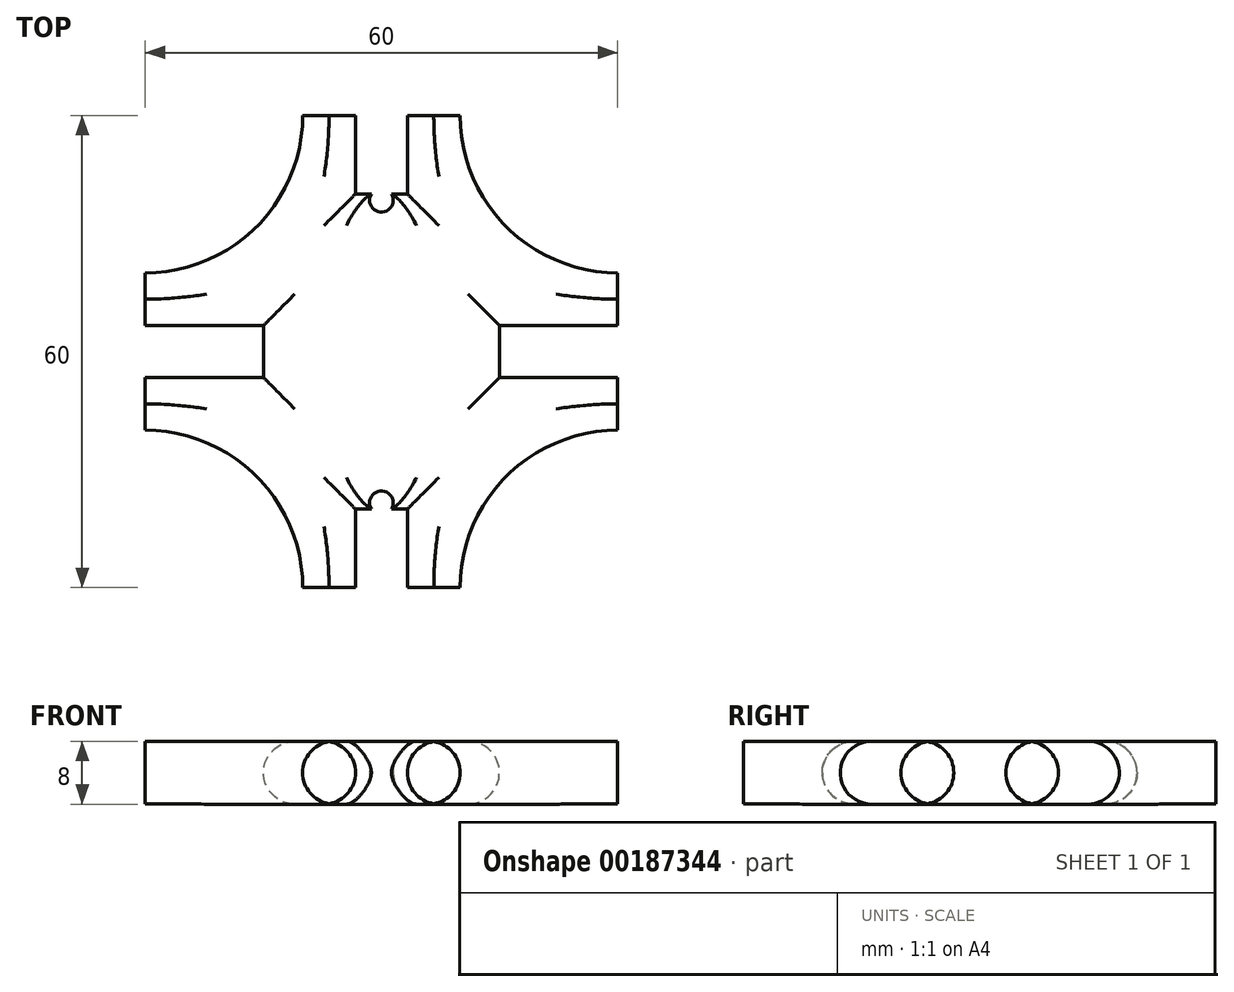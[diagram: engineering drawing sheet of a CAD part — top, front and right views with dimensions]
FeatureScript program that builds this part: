
annotation { "Feature Type Name" : "Feature", "Feature Type Description" : "" }
export const myFeature = defineFeature(function(context is Context, id is Id, definition is map)
    precondition{}
    {
        {
            var Q0;
            Q0=qCreatedBy(makeId("Top.planeOp"),FACE);
            var sketch = newSketch(context, id + "F0", { "sketchPlane" : qUnion([Q0])});
            skLineSegment(sketch, "E0.bottom", {"start": v(10, 30) * mm, "end": v(3.3, 30) * mm});
            skLineSegment(sketch, "E0.top", {"start": v(10, -30) * mm, "end": v(3.3, -30) * mm});
            skLineSegment(sketch, "E0.left", {"start": v(30, 10) * mm, "end": v(30, 3.3) * mm});
            skLineSegment(sketch, "E0.right", {"start": v(-30, 10) * mm, "end": v(-30, 3.3) * mm});
            skPoint(sketch, "E0.middle", {"position": v(0, 0) * mm});
            skArc(sketch, "E1", {"start": v(10, 30) * mm, "mid": v(15.86, 15.86) * mm, "end": v(30, 10) * mm});
            skArc(sketch, "E2", {"start": v(-30, 10) * mm, "mid": v(-15.86, 15.86) * mm, "end": v(-10, 30) * mm});
            skArc(sketch, "E3", {"start": v(-10, -30) * mm, "mid": v(-15.86, -15.86) * mm, "end": v(-30, -10) * mm});
            skArc(sketch, "E4", {"start": v(30, -10) * mm, "mid": v(15.86, -15.86) * mm, "end": v(10, -30) * mm});
            skLineSegment(sketch, "E5.top", {"start": v(-3.3, 20) * mm, "end": v(-1.28, 20) * mm});
            skLineSegment(sketch, "E5.left", {"start": v(-3.3, 30) * mm, "end": v(-3.3, 20) * mm});
            skLineSegment(sketch, "E5.right", {"start": v(3.3, 30) * mm, "end": v(3.3, 20) * mm});
            skArc(sketch, "E6", {"start": v(-1.28, 20) * mm, "mid": v(0, 17.72) * mm, "end": v(1.28, 20) * mm});
            skPoint(sketch, "E6.centerSnap0", {"position": v(0, 20) * mm});
            skLineSegment(sketch, "E7.trimOffspring", {"start": v(1.28, 20) * mm, "end": v(3.3, 20) * mm});
            skLineSegment(sketch, "E8.trimOffspring", {"start": v(-3.3, 30) * mm, "end": v(-10, 30) * mm});
            skLineSegment(sketch, "E9.bottom", {"start": v(3.3, -20) * mm, "end": v(1.28, -20) * mm});
            skLineSegment(sketch, "E9.left", {"start": v(3.3, -20) * mm, "end": v(3.3, -30) * mm});
            skLineSegment(sketch, "E9.right", {"start": v(-3.3, -20) * mm, "end": v(-3.3, -30) * mm});
            skPoint(sketch, "E9.middle", {"position": v(0, -30) * mm});
            skPoint(sketch, "E9.top.end.orphan", {"position": v(-3.3, -40) * mm});
            skPoint(sketch, "E9.top.start.orphan", {"position": v(3.3, -40) * mm});
            skLineSegment(sketch, "E10.trimOffspring", {"start": v(-3.3, -30) * mm, "end": v(-10, -30) * mm});
            skArc(sketch, "E11", {"start": v(1.28, -20) * mm, "mid": v(0, -17.72) * mm, "end": v(-1.28, -20) * mm});
            skLineSegment(sketch, "E12.trimOffspring", {"start": v(-1.28, -20) * mm, "end": v(-3.3, -20) * mm});
            skLineSegment(sketch, "E13.bottom", {"start": v(-15, 3.3) * mm, "end": v(-30, 3.3) * mm});
            skLineSegment(sketch, "E13.top", {"start": v(-15, -3.3) * mm, "end": v(-30, -3.3) * mm});
            skLineSegment(sketch, "E13.left", {"start": v(-15, 3.3) * mm, "end": v(-15, -3.3) * mm});
            skPoint(sketch, "E13.middle", {"position": v(-30, 0) * mm});
            skPoint(sketch, "E13.right.start.orphan", {"position": v(-45, 3.3) * mm});
            skPoint(sketch, "E14.orphan", {"position": v(-45, -3.3) * mm});
            skLineSegment(sketch, "E15.trimOffspring", {"start": v(-30, -3.3) * mm, "end": v(-30, -10) * mm});
            skLineSegment(sketch, "E16.bottom", {"start": v(15, -3.3) * mm, "end": v(30, -3.3) * mm});
            skLineSegment(sketch, "E16.top", {"start": v(15, 3.3) * mm, "end": v(30, 3.3) * mm});
            skLineSegment(sketch, "E16.left", {"start": v(15, -3.3) * mm, "end": v(15, 3.3) * mm});
            skPoint(sketch, "E16.middle", {"position": v(30, 0) * mm});
            skPoint(sketch, "E16.right.end.orphan", {"position": v(45, 3.3) * mm});
            skPoint(sketch, "E17.orphan", {"position": v(45, -3.3) * mm});
            skLineSegment(sketch, "E18.trimOffspring", {"start": v(30, -3.3) * mm, "end": v(30, -10) * mm});
            skSolve(sketch);
        }
        {
            var Q0;
            Q0=makeQuery(id+"F0.imprint","IMPRINT",FACE,{"disambiguationData":[TD([[makeQuery(id+"F0.imprint","IMPRINT",EDGE,{"derivedFrom":sQuery(id+"F0.wireOp",EDGE,"E0.bottom")}),1.0]])]});
            extrude(context, id + "F1", {"entities" : qUnion([Q0]), "depth" : 8 * mm});
        }
        {
            var Q0;
            Q0=makeQuery(id+"F1.opExtrude","CAP_FACE",FACE,{"disambiguationData":[OSD([sQuery(id+"F0.wireOp",EDGE,"E0.bottom"),sQuery(id+"F0.wireOp",EDGE,"E0.top"),sQuery(id+"F0.wireOp",EDGE,"E0.left"),sQuery(id+"F0.wireOp",EDGE,"E0.right"),sQuery(id+"F0.wireOp",EDGE,"E1"),sQuery(id+"F0.wireOp",EDGE,"E2"),sQuery(id+"F0.wireOp",EDGE,"E3"),sQuery(id+"F0.wireOp",EDGE,"E4"),sQuery(id+"F0.wireOp",EDGE,"E5.top"),sQuery(id+"F0.wireOp",EDGE,"E5.left"),sQuery(id+"F0.wireOp",EDGE,"E5.right"),sQuery(id+"F0.wireOp",EDGE,"E6"),sQuery(id+"F0.wireOp",EDGE,"E7.trimOffspring"),sQuery(id+"F0.wireOp",EDGE,"E8.trimOffspring"),sQuery(id+"F0.wireOp",EDGE,"E9.bottom"),sQuery(id+"F0.wireOp",EDGE,"E9.left"),sQuery(id+"F0.wireOp",EDGE,"E9.right"),sQuery(id+"F0.wireOp",EDGE,"E10.trimOffspring"),sQuery(id+"F0.wireOp",EDGE,"E11"),sQuery(id+"F0.wireOp",EDGE,"E12.trimOffspring"),sQuery(id+"F0.wireOp",EDGE,"E13.bottom"),sQuery(id+"F0.wireOp",EDGE,"E13.top"),sQuery(id+"F0.wireOp",EDGE,"E13.left"),sQuery(id+"F0.wireOp",EDGE,"E15.trimOffspring"),sQuery(id+"F0.wireOp",EDGE,"E16.bottom"),sQuery(id+"F0.wireOp",EDGE,"E16.top"),sQuery(id+"F0.wireOp",EDGE,"E16.left"),sQuery(id+"F0.wireOp",EDGE,"E18.trimOffspring")])],"isStart":false});
            var Q1;
            Q1=makeQuery(id+"F1.opExtrude","CAP_FACE",FACE,{"disambiguationData":[OSD([sQuery(id+"F0.wireOp",EDGE,"E0.bottom"),sQuery(id+"F0.wireOp",EDGE,"E0.top"),sQuery(id+"F0.wireOp",EDGE,"E0.left"),sQuery(id+"F0.wireOp",EDGE,"E0.right"),sQuery(id+"F0.wireOp",EDGE,"E1"),sQuery(id+"F0.wireOp",EDGE,"E2"),sQuery(id+"F0.wireOp",EDGE,"E3"),sQuery(id+"F0.wireOp",EDGE,"E4"),sQuery(id+"F0.wireOp",EDGE,"E5.top"),sQuery(id+"F0.wireOp",EDGE,"E5.left"),sQuery(id+"F0.wireOp",EDGE,"E5.right"),sQuery(id+"F0.wireOp",EDGE,"E6"),sQuery(id+"F0.wireOp",EDGE,"E7.trimOffspring"),sQuery(id+"F0.wireOp",EDGE,"E8.trimOffspring"),sQuery(id+"F0.wireOp",EDGE,"E9.bottom"),sQuery(id+"F0.wireOp",EDGE,"E9.left"),sQuery(id+"F0.wireOp",EDGE,"E9.right"),sQuery(id+"F0.wireOp",EDGE,"E10.trimOffspring"),sQuery(id+"F0.wireOp",EDGE,"E11"),sQuery(id+"F0.wireOp",EDGE,"E12.trimOffspring"),sQuery(id+"F0.wireOp",EDGE,"E13.bottom"),sQuery(id+"F0.wireOp",EDGE,"E13.top"),sQuery(id+"F0.wireOp",EDGE,"E13.left"),sQuery(id+"F0.wireOp",EDGE,"E15.trimOffspring"),sQuery(id+"F0.wireOp",EDGE,"E16.bottom"),sQuery(id+"F0.wireOp",EDGE,"E16.top"),sQuery(id+"F0.wireOp",EDGE,"E16.left"),sQuery(id+"F0.wireOp",EDGE,"E18.trimOffspring")])],"isStart":true});
            fillet(context, id + "F2", {"entities" : qUnion([Q0, Q1]), "radius" : 4 * mm, "tangentPropagation" : true, "allowEdgeOverflow" : false});
        }
    });
